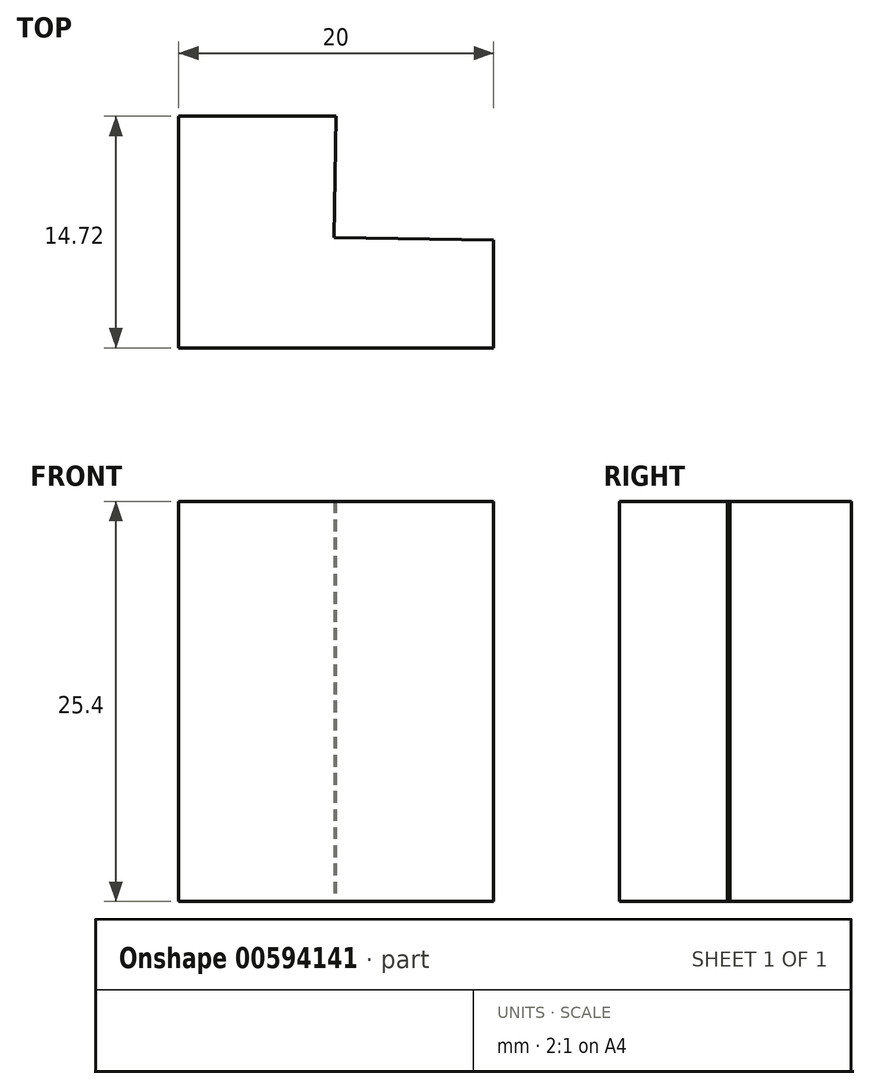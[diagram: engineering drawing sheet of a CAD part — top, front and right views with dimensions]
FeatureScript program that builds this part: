
annotation { "Feature Type Name" : "Feature", "Feature Type Description" : "" }
export const myFeature = defineFeature(function(context is Context, id is Id, definition is map)
    precondition{}
    {
        {
            var Q0;
            Q0=qCreatedBy(makeId("Top.planeOp"),FACE);
            var sketch = newSketch(context, id + "F0", { "sketchPlane" : qUnion([Q0])});
            skLineSegment(sketch, "E0", {"start": v(0, 0) * mm, "end": v(0, 14.72) * mm});
            skLineSegment(sketch, "E1", {"start": v(0, 14.72) * mm, "end": v(10, 14.72) * mm});
            skLineSegment(sketch, "E2", {"start": v(10, 14.72) * mm, "end": v(9.87, 7) * mm});
            skLineSegment(sketch, "E3", {"start": v(9.87, 7) * mm, "end": v(20, 6.84) * mm});
            skLineSegment(sketch, "E4", {"start": v(20, 6.84) * mm, "end": v(20, 0) * mm});
            skLineSegment(sketch, "E5", {"start": v(20, 0) * mm, "end": v(0, 0) * mm});
            skSolve(sketch);
        }
        {
            var Q0;
            Q0=makeQuery(id+"F0.imprint","IMPRINT",FACE,{"disambiguationData":[TD([[makeQuery(id+"F0.imprint","IMPRINT",EDGE,{"derivedFrom":sQuery(id+"F0.wireOp",EDGE,"E0")}),-1.0]])]});
            extrude(context, id + "F1", {"entities" : qUnion([Q0]), "depth" : 25.4 * mm, "offsetDistance" : 25.4 * mm});
        }
    });
